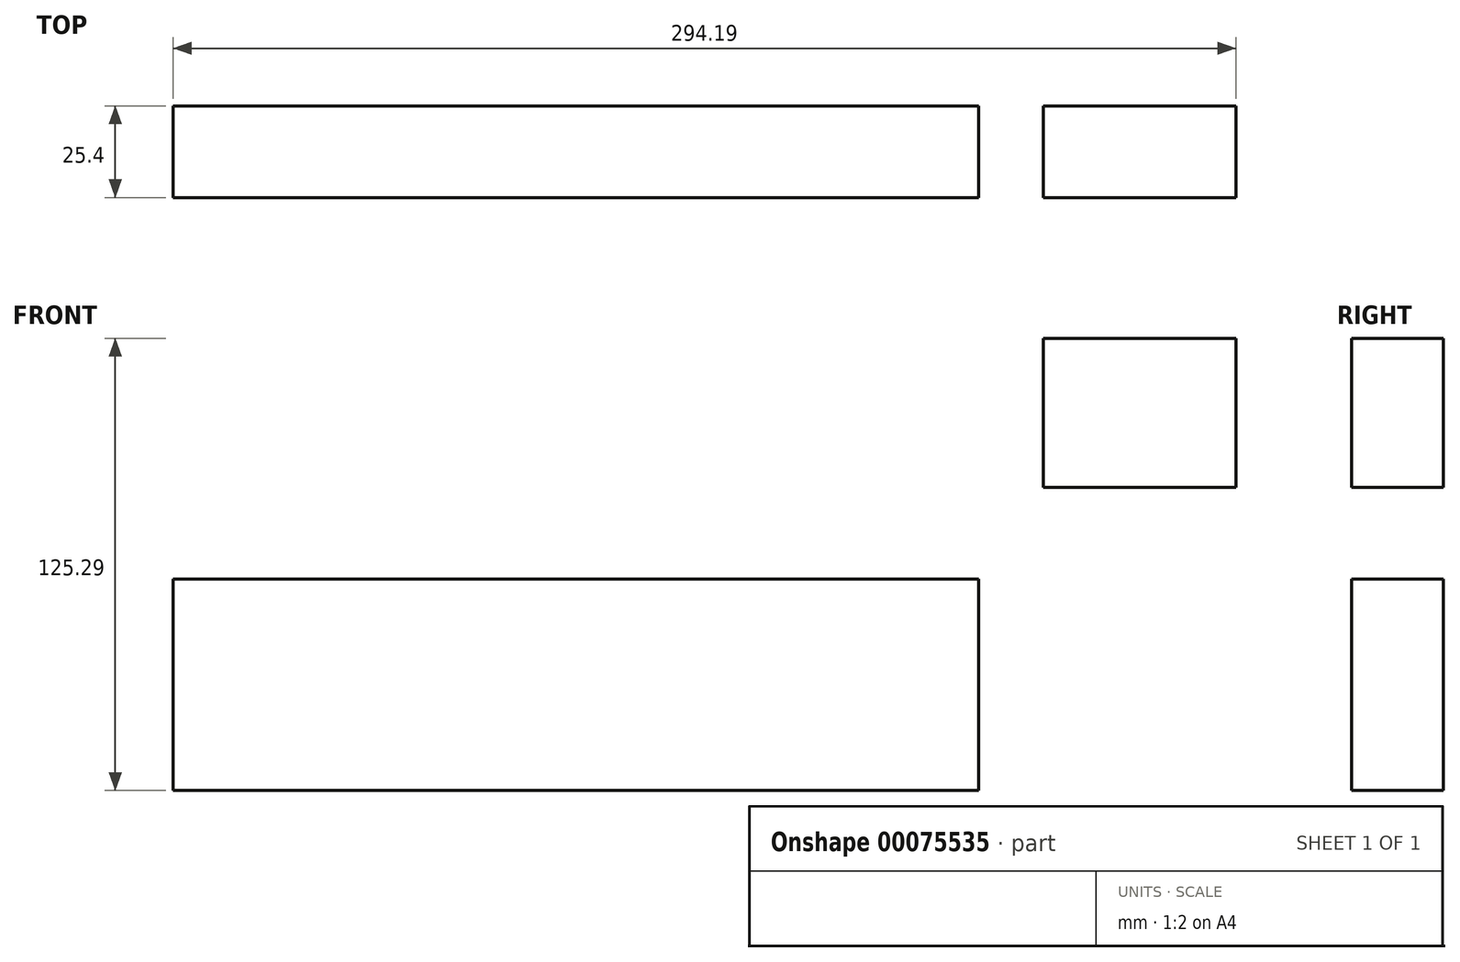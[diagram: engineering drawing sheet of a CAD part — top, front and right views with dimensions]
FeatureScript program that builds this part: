
annotation { "Feature Type Name" : "Feature", "Feature Type Description" : "" }
export const myFeature = defineFeature(function(context is Context, id is Id, definition is map)
    precondition{}
    {
        {
            var Q0;
            Q0=qCreatedBy(makeId("Front.planeOp"),FACE);
            var sketch = newSketch(context, id + "F0", { "sketchPlane" : qUnion([Q0])});
            skLineSegment(sketch, "E0.bottom", {"start": v(-113.43, 22.41) * mm, "end": v(109.56, 22.41) * mm});
            skLineSegment(sketch, "E0.top", {"start": v(-113.43, -36.23) * mm, "end": v(109.56, -36.23) * mm});
            skLineSegment(sketch, "E0.left", {"start": v(-113.43, 22.41) * mm, "end": v(-113.43, -36.23) * mm});
            skLineSegment(sketch, "E0.right", {"start": v(109.56, 22.41) * mm, "end": v(109.56, -36.23) * mm});
            skLineSegment(sketch, "E1.bottom", {"start": v(127.43, 47.81) * mm, "end": v(180.76, 47.81) * mm});
            skLineSegment(sketch, "E1.top", {"start": v(127.43, 89.06) * mm, "end": v(180.76, 89.06) * mm});
            skLineSegment(sketch, "E1.left", {"start": v(127.43, 47.81) * mm, "end": v(127.43, 89.06) * mm});
            skLineSegment(sketch, "E1.right", {"start": v(180.76, 47.81) * mm, "end": v(180.76, 89.06) * mm});
            skLineSegment(sketch, "E2", {"start": v(109.56, 22.41) * mm, "end": v(109.56, 47.81) * mm});
            skLineSegment(sketch, "E3", {"start": v(109.56, 47.81) * mm, "end": v(127.43, 47.81) * mm});
            skSolve(sketch);
        }
        {
            var Q0;
            Q0 = qSketchRegion(id + "F0", true);
            extrude(context, id + "F1", {"entities" : qUnion([Q0]), "depth" : 25.4 * mm});
        }
    });
